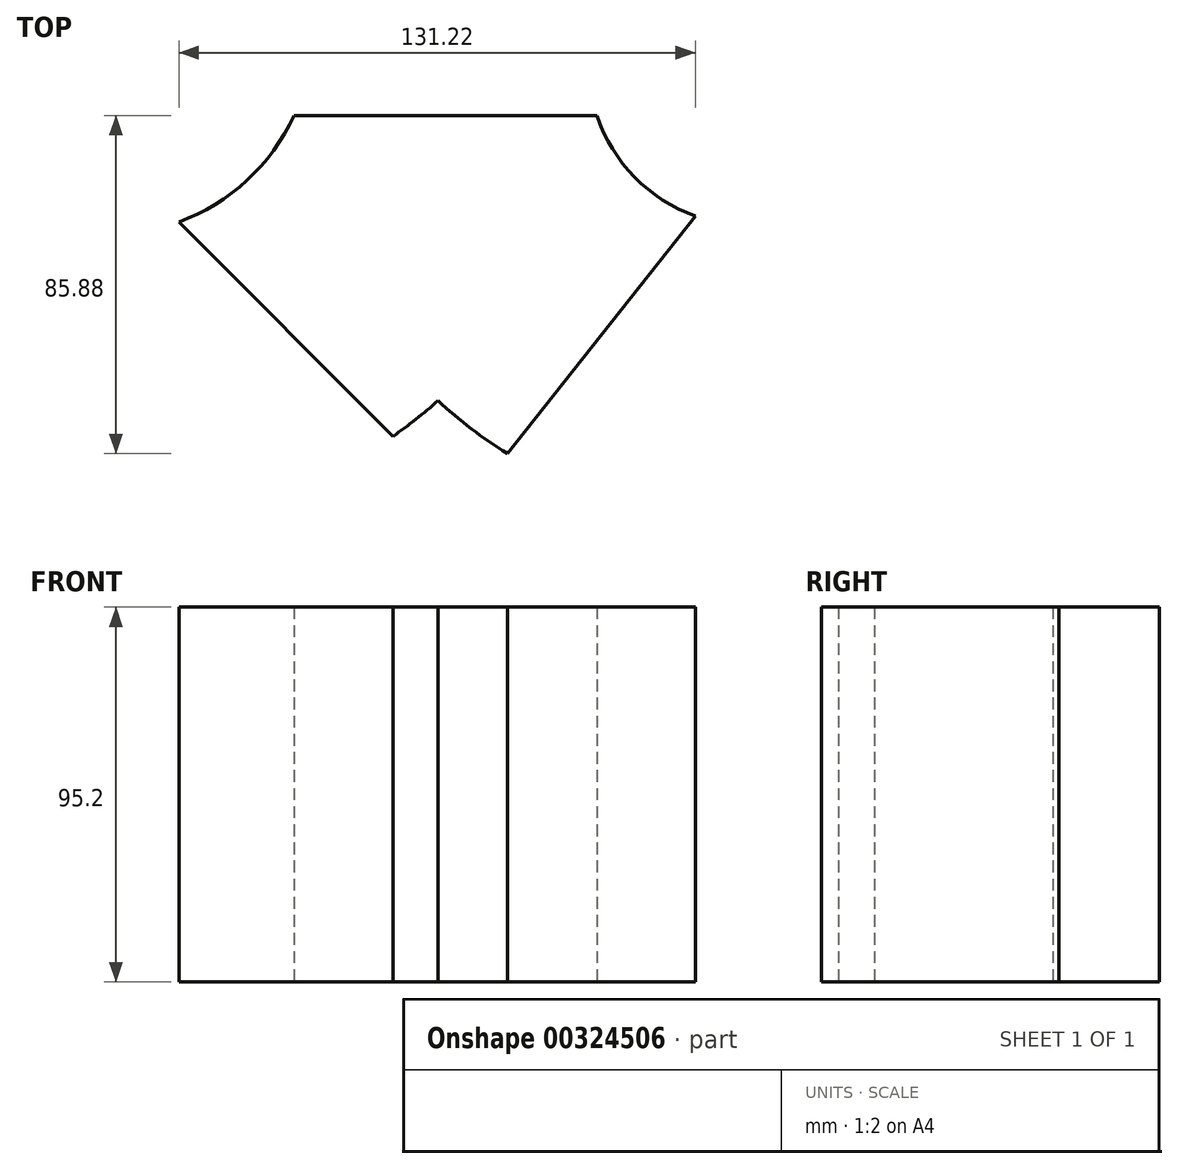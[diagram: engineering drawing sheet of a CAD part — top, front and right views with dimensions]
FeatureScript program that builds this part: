
annotation { "Feature Type Name" : "Feature", "Feature Type Description" : "" }
export const myFeature = defineFeature(function(context is Context, id is Id, definition is map)
    precondition{}
    {
        {
            var Q0;
            Q0=qCreatedBy(makeId("Front.planeOp"),FACE);
            var sketch = newSketch(context, id + "F0", { "sketchPlane" : qUnion([Q0])});
            skPoint(sketch, "E0.middle", {"position": v(-0.29, 0.43) * mm});
            skPoint(sketch, "E0.bottom.start.orphan", {"position": v(-38.49, 47.6) * mm});
            skPoint(sketch, "E0.right.start.orphan", {"position": v(37.9, 47.6) * mm});
            skPoint(sketch, "E0.top.end.orphan", {"position": v(37.9, -46.73) * mm});
            skPoint(sketch, "E0.top.start.orphan", {"position": v(-38.49, -46.73) * mm});
            skLineSegment(sketch, "E1.bottom", {"start": v(-38.49, 47.6) * mm, "end": v(38.49, 47.6) * mm});
            skLineSegment(sketch, "E1.top", {"start": v(-38.49, -47.6) * mm, "end": v(38.49, -47.6) * mm});
            skLineSegment(sketch, "E1.left", {"start": v(-38.49, 47.6) * mm, "end": v(-38.49, -47.6) * mm});
            skLineSegment(sketch, "E1.right", {"start": v(38.49, 47.6) * mm, "end": v(38.49, -47.6) * mm});
            skPoint(sketch, "E1.middle", {"position": v(0, 0) * mm});
            skSolve(sketch);
        }
        {
            var Q0;
            Q0=qCreatedBy(makeId("Top.planeOp"),FACE);
            var sketch = newSketch(context, id + "F1", { "sketchPlane" : qUnion([Q0])});
            skArc(sketch, "E2", {"start": v(0, 0) * mm, "mid": v(13.44, -32.4) * mm, "end": v(39.64, -55.7) * mm});
            skArc(sketch, "E3", {"start": v(-40.51, -54.26) * mm, "mid": v(-14.85, -31.16) * mm, "end": v(0, 0) * mm});
            skCircle(sketch, "E4", {"center": v(0, 0) * mm, "radius": 25.33 * mm});
            skSolve(sketch);
        }
        {
            var Q0;
            Q0=makeQuery(id+"F0.imprint","IMPRINT",FACE,{"disambiguationData":[TD([[makeQuery(id+"F0.imprint","IMPRINT",EDGE,{"derivedFrom":sQuery(id+"F0.wireOp",EDGE,"kHKDYk5W-tVrx-WuCs-vkZz-NPrd69m5xJw7")}),1.0]])]});
            var Q1;
            Q1=makeQuery(id+"F0.imprint","IMPRINT",FACE,{"disambiguationData":[TD([[makeQuery(id+"F0.imprint","IMPRINT",EDGE,{"derivedFrom":sQuery(id+"F0.wireOp",EDGE,"E1.bottom")}),-1.0]])]});
            var Q2;
            Q2=sQuery(id+"F1.wireOp",EDGE,"E2");
            sweep(context, id + "F2", {"profiles" : qUnion([Q0, Q1]), "path" : qUnion([Q2])});
        }
        {
            var Q0;
            Q0=makeQuery(id+"F0.imprint","IMPRINT",FACE,{"disambiguationData":[TD([[makeQuery(id+"F0.imprint","IMPRINT",EDGE,{"derivedFrom":sQuery(id+"F0.wireOp",EDGE,"E1.bottom")}),-1.0]])]});
            var Q1;
            Q1=sQuery(id+"F1.wireOp",EDGE,"E3");
            sweep(context, id + "F3", {"operationType" : NewBodyOperationType.ADD, "profiles" : qUnion([Q0]), "path" : qUnion([Q1])});
        }
        {
            var Q0;
            Q0=sQuery(id+"F1.wireOp",EDGE,"E4");
            extrude(context, id + "F4", {"bodyType" : ToolBodyType.SURFACE, "surfaceEntities" : qUnion([Q0]), "depth" : 47.5 * mm, "hasSecondDirection" : true, "secondDirectionOppositeDirection" : true, "secondDirectionDepth" : 47 * mm});
        }
    });
